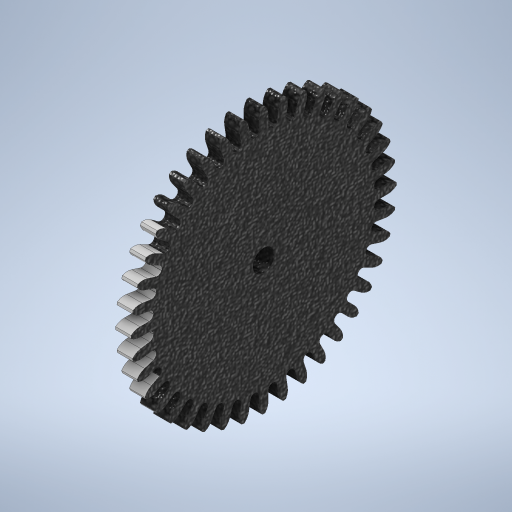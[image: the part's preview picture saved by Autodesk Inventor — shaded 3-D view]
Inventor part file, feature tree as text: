
AUTODESK INVENTOR PART (.ipt)
format: ipt  version: 2024 (Build 280153020, 153B)  size: 859,648 bytes
history: native  units: mm
features: extrude x1, sketch x1
ambient origin geometry x8: Origin, YZ Plane, XZ Plane, XY Plane, X Axis, Y Axis, Z Axis, Center Point
bodies: Body1 (feature_tree)
feature tree (2):
  extrude  "Extrusion2"  Depth=3.5mm
  sketch  "Sketch1"  dims[d0=5.0mm d1=50.0mm d2=3.0mm d3=2.0mm d4=1.570796mm d5=0.785398mm d7=2.04mm d8=1.02mm d9=0.3mm d10=0.6mm d11=3.0mm d12=3.0mm d13=1.0mm d14=400.0mm d16=360.0deg d20=3.5mm d21=0.0mm]
